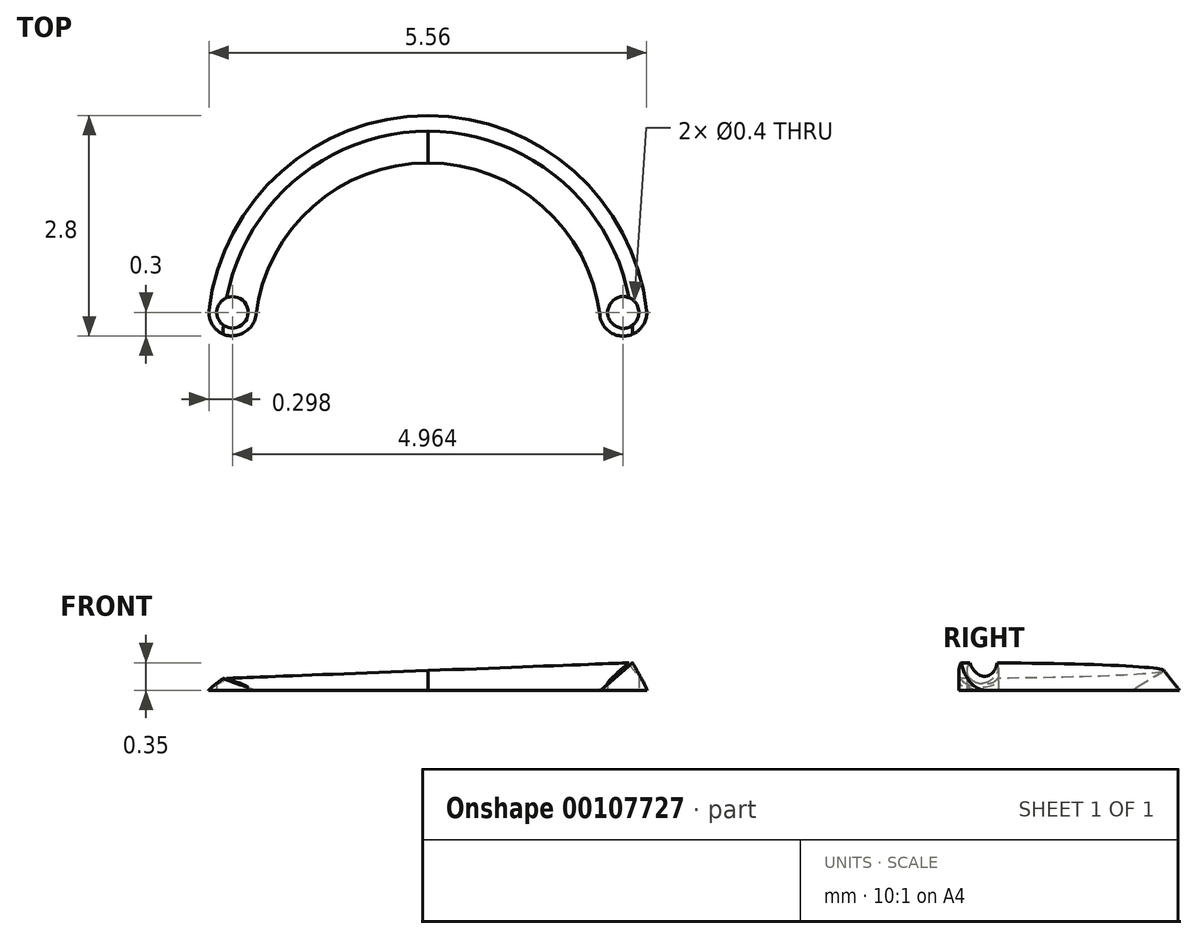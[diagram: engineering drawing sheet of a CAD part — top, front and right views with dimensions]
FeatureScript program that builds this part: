
annotation { "Feature Type Name" : "Feature", "Feature Type Description" : "" }
export const myFeature = defineFeature(function(context is Context, id is Id, definition is map)
    precondition{}
    {
        {
            var Q0;
            Q0=qCreatedBy(makeId("Top.planeOp"),FACE);
            var sketch = newSketch(context, id + "F0", { "sketchPlane" : qUnion([Q0])});
            skCircle(sketch, "E0", {"center": v(0, 0) * mm, "radius": 2.2 * mm, "construction": true});
            skCircle(sketch, "E1", {"center": v(0, 0) * mm, "radius": 2.8 * mm, "construction": true});
            skCircle(sketch, "E2", {"center": v(-2.48, 0.3) * mm, "radius": 0.3 * mm, "construction": true});
            skPoint(sketch, "E2.first.point", {"position": v(-2.18, 0.26) * mm});
            skPoint(sketch, "E2.second.point", {"position": v(-2.78, 0.34) * mm});
            skPoint(sketch, "E2.third.point", {"position": v(-2.48, 0) * mm});
            skCircle(sketch, "E3", {"center": v(2.48, 0.3) * mm, "radius": 0.3 * mm, "construction": true});
            skPoint(sketch, "E3.first.point", {"position": v(2.18, 0.26) * mm});
            skPoint(sketch, "E3.second.point", {"position": v(2.78, 0.34) * mm});
            skPoint(sketch, "E3.third.point", {"position": v(2.48, 0) * mm});
            skLineSegment(sketch, "E4", {"start": v(0, 0) * mm, "end": v(-2.78, 0.34) * mm, "construction": true});
            skLineSegment(sketch, "E5", {"start": v(0, 0) * mm, "end": v(2.78, 0.34) * mm, "construction": true});
            skSolve(sketch);
        }
        {
            var Q0;
            Q0=qCreatedBy(makeId("Front.planeOp"),FACE);
            var sketch = newSketch(context, id + "F1", { "sketchPlane" : qUnion([Q0])});
            skLineSegment(sketch, "E6", {"start": v(-2.8, 0) * mm, "end": v(-2.6, 0.15) * mm});
            skLineSegment(sketch, "E7", {"start": v(-2.6, 0.15) * mm, "end": v(-2.2, 0) * mm});
            skLineSegment(sketch, "E8", {"start": v(-2.2, 0) * mm, "end": v(-2.8, 0) * mm});
            skSolve(sketch);
        }
        {
            var Q0;
            Q0=qCreatedBy(makeId("Front.planeOp"),FACE);
            var sketch = newSketch(context, id + "F2", { "sketchPlane" : qUnion([Q0])});
            skLineSegment(sketch, "E9", {"start": v(2.8, 0) * mm, "end": v(2.6, 0.35) * mm});
            skLineSegment(sketch, "E10", {"start": v(2.6, 0.35) * mm, "end": v(2.2, 0) * mm});
            skLineSegment(sketch, "E11", {"start": v(2.2, 0) * mm, "end": v(2.8, 0) * mm});
            skSolve(sketch);
        }
        {
            var Q0;
            Q0=qCreatedBy(makeId("Front.planeOp"),FACE);
            var sketch = newSketch(context, id + "F3", { "sketchPlane" : qUnion([Q0])});
            skLineSegment(sketch, "E12", {"start": v(-2.6, 0.15) * mm, "end": v(2.6, 0.35) * mm, "construction": true});
            skSolve(sketch);
        }
        {
            var Q0;
            Q0=sQuery(id+"F3.wireOp",EDGE,"E12");
            cPlane(context, id + "F4", {"entities" : qUnion([Q0]), "cplaneType" : CPlaneType.LINE_ANGLE, "offset" : 25 * mm, "angle" : 90 * degree, "width" : 150 * mm, "height" : 150 * mm});
        }
        {
            var Q0;
            Q0=qCreatedBy(id+"F4.planeOp",FACE);
            var sketch = newSketch(context, id + "F5", { "sketchPlane" : qUnion([Q0])});
            skArc(sketch, "E13", {"start": v(2.61, 0) * mm, "mid": v(0, 2.6) * mm, "end": v(-2.6, 0) * mm, "construction": true});
            skSolve(sketch);
        }
        {
            var Q0;
            Q0=qCreatedBy(makeId("Right.planeOp"),FACE);
            var sketch = newSketch(context, id + "F6", { "sketchPlane" : qUnion([Q0])});
            skLineSegment(sketch, "E14", {"start": v(2.2, 0) * mm, "end": v(2.6, 0.25) * mm});
            skLineSegment(sketch, "E15", {"start": v(2.6, 0.25) * mm, "end": v(2.8, 0) * mm});
            skLineSegment(sketch, "E16", {"start": v(2.8, 0) * mm, "end": v(2.2, 0) * mm});
            skSolve(sketch);
        }
        {
            var Q0;
            Q0=qCreatedBy(id+"F4.planeOp",FACE);
            var sketch = newSketch(context, id + "F7", { "sketchPlane" : qUnion([Q0])});
            skArc(sketch, "E17", {"start": v(0, 2.6) * mm, "mid": v(-1.83, 1.84) * mm, "end": v(-2.6, 0) * mm});
            skSolve(sketch);
        }
        {
            var Q0;
            Q0=qCreatedBy(makeId("Top.planeOp"),FACE);
            var sketch = newSketch(context, id + "F8", { "sketchPlane" : qUnion([Q0])});
            skArc(sketch, "E18", {"start": v(0, 2.2) * mm, "mid": v(-1.56, 1.56) * mm, "end": v(-2.2, 0) * mm});
            skArc(sketch, "E19", {"start": v(0, 2.8) * mm, "mid": v(-1.98, 1.98) * mm, "end": v(-2.8, 0) * mm});
            skSolve(sketch);
        }
        {
            var Q0;
            Q0 = qSketchRegion(id + "F1", true);
            var Q1;
            Q1 = qSketchRegion(id + "F6", true);
            var Q2;
            Q2=sQuery(id+"F7.wireOp",EDGE,"E17");
            var Q3;
            Q3=sQuery(id+"F8.wireOp",EDGE,"E19");
            var Q4;
            Q4=sQuery(id+"F8.wireOp",EDGE,"E18");
            loft(context, id + "F9", {"addGuides" : true, "sheetProfilesArray" : [{ "sheetProfileEntities" : qUnion([Q0]) }, { "sheetProfileEntities" : qUnion([Q1]) }], "guidesArray" : [{ "guideEntities" : qUnion([Q2]), "guideDerivativeType" : LoftGuideDerivativeType.DEFAULT, "guideDerivativeMagnitude" : 1 }, { "guideEntities" : qUnion([Q3]), "guideDerivativeType" : LoftGuideDerivativeType.DEFAULT, "guideDerivativeMagnitude" : 1 }, { "guideEntities" : qUnion([Q4]), "guideDerivativeType" : LoftGuideDerivativeType.DEFAULT, "guideDerivativeMagnitude" : 1 }]});
        }
        {
            var Q0;
            Q0=qCreatedBy(id+"F4.planeOp",FACE);
            var sketch = newSketch(context, id + "F10", { "sketchPlane" : qUnion([Q0])});
            skArc(sketch, "E20", {"start": v(2.61, 0) * mm, "mid": v(1.85, 1.84) * mm, "end": v(0, 2.6) * mm});
            skSolve(sketch);
        }
        {
            var Q0;
            Q0=qCreatedBy(makeId("Top.planeOp"),FACE);
            var sketch = newSketch(context, id + "F11", { "sketchPlane" : qUnion([Q0])});
            skArc(sketch, "E21", {"start": v(2.2, 0) * mm, "mid": v(1.56, 1.56) * mm, "end": v(0, 2.2) * mm});
            skArc(sketch, "E22", {"start": v(2.8, 0) * mm, "mid": v(1.98, 1.98) * mm, "end": v(0, 2.8) * mm});
            skSolve(sketch);
        }
        {
            var Q1;
            Q1 = qSketchRegion(id + "F6", true);
            var Q2;
            Q2 = qSketchRegion(id + "F2", true);
            var Q3;
            Q3=sQuery(id+"F11.wireOp",EDGE,"E21");
            var Q4;
            Q4=sQuery(id+"F10.wireOp",EDGE,"E20");
            var Q5;
            Q5=sQuery(id+"F11.wireOp",EDGE,"E22");
            loft(context, id + "F12", {"operationType" : NewBodyOperationType.ADD, "addGuides" : true, "sheetProfilesArray" : [{ "sheetProfileEntities" : qUnion([Q1]) }, { "sheetProfileEntities" : qUnion([Q2]) }], "guidesArray" : [{ "guideEntities" : qUnion([Q3]), "guideDerivativeType" : LoftGuideDerivativeType.DEFAULT, "guideDerivativeMagnitude" : 1 }, { "guideEntities" : qUnion([Q4]), "guideDerivativeType" : LoftGuideDerivativeType.DEFAULT, "guideDerivativeMagnitude" : 1 }, { "guideEntities" : qUnion([Q5]), "guideDerivativeType" : LoftGuideDerivativeType.DEFAULT, "guideDerivativeMagnitude" : 1 }]});
        }
        {
            var Q0;
            {var subQ0=sQuery(id+"F6.wireOp",EDGE,"E16");Q0=makeQuery(id+"F12.boolean.opBoolean","MERGE",FACE,{"derivedFrom":[makeQuery(id+"F9.opLoft","SWEPT_FACE",FACE,{"disambiguationData":[OSD([sQuery(id+"F1.wireOp",EDGE,"E8"),subQ0,sQuery(id+"F8.wireOp",EDGE,"E18"),sQuery(id+"F8.wireOp",EDGE,"E19")])]}),makeQuery(id+"F12.opLoft","SWEPT_FACE",FACE,{"disambiguationData":[OSD([sQuery(id+"F2.wireOp",EDGE,"E9"),sQuery(id+"F2.wireOp",EDGE,"E11"),subQ0,sQuery(id+"F11.wireOp",EDGE,"E21"),sQuery(id+"F11.wireOp",EDGE,"E22")])]})]});}
            var sketch = newSketch(context, id + "F13", { "sketchPlane" : qUnion([Q0])});
            skCircle(sketch, "E23", {"center": v(-2.48, -0.3) * mm, "radius": 0.2 * mm});
            skCircle(sketch, "E24", {"center": v(2.48, -0.3) * mm, "radius": 0.2 * mm});
            skSolve(sketch);
        }
        {
            var Q0;
            Q0=qCreatedBy(makeId("Top.planeOp"),FACE);
            var sketch = newSketch(context, id + "F14", { "sketchPlane" : qUnion([Q0])});
            skArc(sketch, "E25", {"start": v(-2.78, 0.34) * mm, "mid": v(-2.52, 0) * mm, "end": v(-2.18, 0.26) * mm});
            skArc(sketch, "E26", {"start": v(-2.78, 0.34) * mm, "mid": v(-2.8, 0.17) * mm, "end": v(-2.8, 0) * mm});
            skArc(sketch, "E27", {"start": v(-2.18, 0.26) * mm, "mid": v(-2.2, 0.13) * mm, "end": v(-2.2, 0) * mm});
            skLineSegment(sketch, "E28", {"start": v(-2.8, 0) * mm, "end": v(-2.2, 0) * mm});
            skLineSegment(sketch, "E29", {"start": v(0, 0) * mm, "end": v(0, 2.2) * mm, "construction": true});
            skArc(sketch, "E30.MirrorCS", {"start": v(2.18, 0.26) * mm, "mid": v(2.2, 0.13) * mm, "end": v(2.2, 0) * mm});
            skArc(sketch, "E31.MirrorCS", {"start": v(2.78, 0.34) * mm, "mid": v(2.52, 0) * mm, "end": v(2.18, 0.26) * mm});
            skArc(sketch, "E32.MirrorCS", {"start": v(2.78, 0.34) * mm, "mid": v(2.8, 0.17) * mm, "end": v(2.8, 0) * mm});
            skLineSegment(sketch, "E33.MirrorCS", {"start": v(2.8, 0) * mm, "end": v(2.2, 0) * mm});
            skSolve(sketch);
        }
        {
            var Q0;
            Q0 = qSketchRegion(id + "F14", true);
            extrude(context, id + "F15", {"entities" : qUnion([Q0]), "operationType" : NewBodyOperationType.REMOVE, "endBound" : BoundingType.THROUGH_ALL, "depth" : 25 * mm});
        }
        {
            var Q0;
            Q0 = qSketchRegion(id + "F13", true);
            extrude(context, id + "F16", {"entities" : qUnion([Q0]), "operationType" : NewBodyOperationType.REMOVE, "endBound" : BoundingType.THROUGH_ALL, "oppositeDirection" : true, "depth" : 25 * mm});
        }
    });
